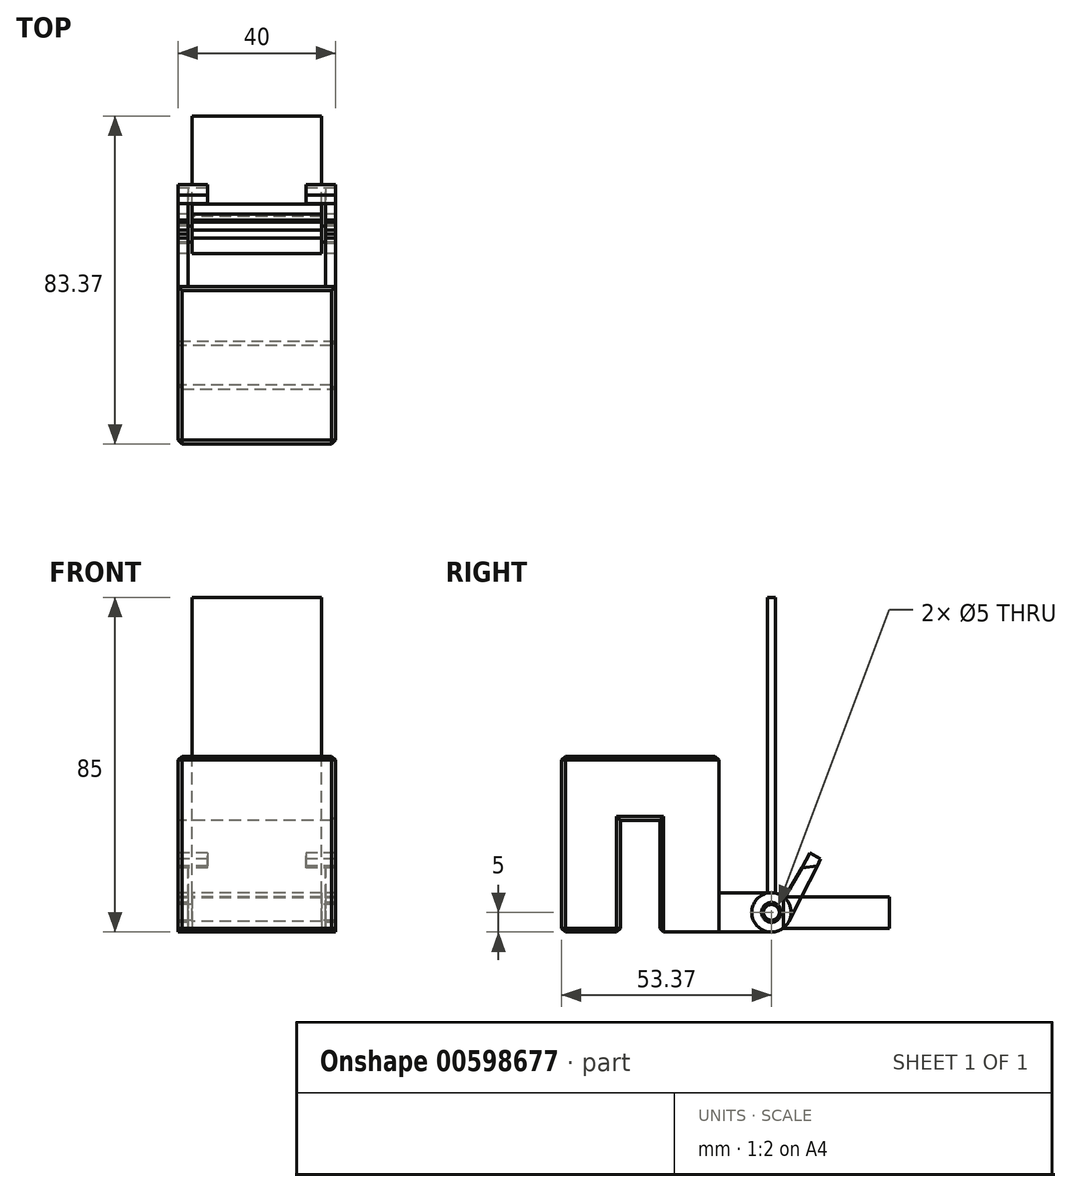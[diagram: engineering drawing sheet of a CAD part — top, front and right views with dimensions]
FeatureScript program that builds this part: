
annotation { "Feature Type Name" : "Feature", "Feature Type Description" : "" }
export const myFeature = defineFeature(function(context is Context, id is Id, definition is map)
    precondition{}
    {
        {
            var Q0;
            Q0=qCreatedBy(makeId("Right.planeOp"),FACE);
            var sketch = newSketch(context, id + "F0", { "sketchPlane" : qUnion([Q0])});
            skCircle(sketch, "E0", {"center": v(0, 0) * mm, "radius": 2.5 * mm});
            skArc(sketch, "E1", {"start": v(0, -5) * mm, "mid": v(5, 0) * mm, "end": v(0, 5) * mm});
            skLineSegment(sketch, "E2.bottom", {"start": v(0, 5) * mm, "end": v(-13.37, 5) * mm});
            skLineSegment(sketch, "E2.top", {"start": v(0, -5) * mm, "end": v(-28.37, -5) * mm});
            skLineSegment(sketch, "E2.right", {"start": v(-53.37, 5) * mm, "end": v(-53.37, -5) * mm});
            skLineSegment(sketch, "E3.top", {"start": v(-53.37, 39.68) * mm, "end": v(-13.37, 39.68) * mm});
            skLineSegment(sketch, "E3.left", {"start": v(-53.37, 5) * mm, "end": v(-53.37, 39.68) * mm});
            skLineSegment(sketch, "E3.right", {"start": v(-13.37, 5) * mm, "end": v(-13.37, 39.68) * mm});
            skLineSegment(sketch, "E4.top", {"start": v(-38.37, 23.37) * mm, "end": v(-28.37, 23.37) * mm});
            skLineSegment(sketch, "E4.left", {"start": v(-38.37, -5) * mm, "end": v(-38.37, 23.37) * mm});
            skLineSegment(sketch, "E4.right", {"start": v(-28.37, -5) * mm, "end": v(-28.37, 23.37) * mm});
            skLineSegment(sketch, "E5.trimOffspring", {"start": v(-38.37, -5) * mm, "end": v(-53.37, -5) * mm});
            skLineSegment(sketch, "E6", {"start": v(-38.37, 23.37) * mm, "end": v(-53.37, 23.37) * mm, "construction": true});
            skLineSegment(sketch, "E7", {"start": v(-28.37, 23.37) * mm, "end": v(-13.37, 23.37) * mm, "construction": true});
            skCircle(sketch, "E8", {"center": v(0, 0) * mm, "radius": 5 * mm});
            skLineSegment(sketch, "E9.bottom", {"start": v(1, 4.9) * mm, "end": v(-1, 4.9) * mm});
            skLineSegment(sketch, "E9.top", {"start": v(1, 80) * mm, "end": v(-1, 80) * mm});
            skLineSegment(sketch, "E9.left", {"start": v(1, 4.9) * mm, "end": v(1, 80) * mm});
            skLineSegment(sketch, "E9.right", {"start": v(-1, 4.9) * mm, "end": v(-1, 80) * mm});
            skPoint(sketch, "E9.middle", {"position": v(0, 42.45) * mm});
            skLineSegment(sketch, "E10.bottom", {"start": v(3, 4) * mm, "end": v(30, 4) * mm});
            skLineSegment(sketch, "E10.top", {"start": v(3, -4) * mm, "end": v(30, -4) * mm});
            skLineSegment(sketch, "E10.left", {"start": v(3, 4) * mm, "end": v(3, -4) * mm});
            skLineSegment(sketch, "E10.right", {"start": v(30, 4) * mm, "end": v(30, -4) * mm});
            skPoint(sketch, "E10.middle", {"position": v(16.5, 0) * mm});
            skCircle(sketch, "E11", {"center": v(0, 0) * mm, "radius": 2 * mm});
            skLineSegment(sketch, "E12", {"start": v(-13.37, 5) * mm, "end": v(-13.37, -5) * mm});
            skLineSegment(sketch, "E13", {"start": v(0, 0) * mm, "end": v(9.94, 17.21) * mm, "construction": true});
            skLineSegment(sketch, "E14", {"start": v(3.32, 3.74) * mm, "end": v(9.85, 15.06) * mm});
            skLineSegment(sketch, "E15", {"start": v(6.53, 11.32) * mm, "end": v(7.4, 10.82) * mm, "construction": true});
            skLineSegment(sketch, "E16", {"start": v(1, 16.02) * mm, "end": v(0, 16.02) * mm, "construction": true});
            skLineSegment(sketch, "E17", {"start": v(9.85, 15.06) * mm, "end": v(12.5, 13.53) * mm});
            skLineSegment(sketch, "E18", {"start": v(12.5, 13.53) * mm, "end": v(4.46, -2.27) * mm});
            skLineSegment(sketch, "E19", {"start": v(7.7, 11.33) * mm, "end": v(11.64, 11.85) * mm});
            skSolve(sketch);
        }
        {
            var Q0;
            {var subQ4=sQuery(id+"F0.wireOp",EDGE,"E2.top");Q0=makeQuery(id+"F0.imprint","IMPRINT",FACE,{"disambiguationData":[TD([[makeQuery(id+"F0.imprint","IMPRINT",EDGE,{"derivedFrom":subQ4}),-1.0]])]});}
            var Q1;
            Q1=makeQuery(id+"F0.imprint","IMPRINT",FACE,{"disambiguationData":[TD([[makeQuery(id+"F0.imprint","IMPRINT",EDGE,{"derivedFrom":sQuery(id+"F0.wireOp",EDGE,"E0")}),-1.0]])]});
            var Q2;
            {var subQ2=sQuery(id+"F0.wireOp",EDGE,"E9.bottom");Q2=makeQuery(id+"F0.imprint","IMPRINT",FACE,{"disambiguationData":[TD([[makeQuery(id+"F0.imprint","IMPRINT",EDGE,{"derivedFrom":subQ2}),-1.0]])]});}
            var Q3;
            {var subQ0=sQuery(id+"F0.wireOp",EDGE,"E8");var subQ1=sQuery(id+"F0.wireOp",EDGE,"E2.bottom");var subQ2=makeQuery(id+"F0.imprint","INTERSECT",VERTEX,{"derivedFrom":[subQ1,subQ0]});Q3=makeQuery(id+"F0.imprint","IMPRINT",FACE,{"disambiguationData":[TD([[makeQuery(id+"F0.imprint","IMPRINT",EDGE,{"disambiguationData":[TD([[subQ2,-1.0]])],"derivedFrom":subQ1}),1.0]])]});}
            var Q4;
            {var subQ0=sQuery(id+"F0.wireOp",EDGE,"E10.left");Q4=makeQuery(id+"F0.imprint","IMPRINT",FACE,{"disambiguationData":[TD([[makeQuery(id+"F0.imprint","IMPRINT",EDGE,{"derivedFrom":subQ0}),1.0]])]});}
            var Q5;
            Q5=makeQuery(id+"F0.imprint","IMPRINT",FACE,{"disambiguationData":[TD([[makeQuery(id+"F0.imprint","IMPRINT",EDGE,{"derivedFrom":sQuery(id+"F0.wireOp",EDGE,"E2.right")}),1.0]])]});
            var Q6;
            {var subQ1=sQuery(id+"F0.wireOp",EDGE,"E8");var subQ3=sQuery(id+"F0.wireOp",EDGE,"pCUO0WgF-IgAN-LRAv-omMa-FBrBm6pz1iVL");var subQ4=makeQuery(id+"F0.imprint","INTERSECT",VERTEX,{"derivedFrom":[subQ1,subQ3]});Q6=makeQuery(id+"F0.imprint","IMPRINT",FACE,{"disambiguationData":[TD([[makeQuery(id+"F0.imprint","IMPRINT",EDGE,{"disambiguationData":[TD([[subQ4,1.0]])],"derivedFrom":subQ3}),-1.0]])]});}
            var Q7;
            {var subQ0=sQuery(id+"F0.wireOp",EDGE,"0aa6f748-86be-4359-a253-0a0e9de2a2ff.0");Q7=makeQuery(id+"F0.imprint","IMPRINT",FACE,{"disambiguationData":[TD([[makeQuery(id+"F0.imprint","IMPRINT",EDGE,{"derivedFrom":subQ0}),-1.0]])]});}
            var Q8;
            {var subQ0=sQuery(id+"F0.wireOp",EDGE,"HSa4Dfjx-L4mI-NIt9-n0gS-I4i8fd6hyLie");Q8=makeQuery(id+"F0.imprint","IMPRINT",FACE,{"disambiguationData":[TD([[makeQuery(id+"F0.imprint","IMPRINT",EDGE,{"derivedFrom":subQ0}),-1.0]])]});}
            var Q9;
            {var subQ1=sQuery(id+"F0.wireOp",EDGE,"E8");var subQ3=sQuery(id+"F0.wireOp",EDGE,"E14");var subQ4=makeQuery(id+"F0.imprint","INTERSECT",VERTEX,{"derivedFrom":[subQ1,subQ3]});Q9=makeQuery(id+"F0.imprint","IMPRINT",FACE,{"disambiguationData":[TD([[makeQuery(id+"F0.imprint","IMPRINT",EDGE,{"disambiguationData":[TD([[subQ4,-1.0]])],"derivedFrom":subQ3}),1.0]])]});}
            var Q10;
            {var subQ0=sQuery(id+"F0.wireOp",EDGE,"E14");var subQ1=sQuery(id+"F0.wireOp",EDGE,"E8");var subQ2=makeQuery(id+"F0.imprint","INTERSECT",VERTEX,{"derivedFrom":[subQ1,subQ0]});Q10=makeQuery(id+"F0.imprint","IMPRINT",FACE,{"disambiguationData":[TD([[makeQuery(id+"F0.imprint","IMPRINT",EDGE,{"disambiguationData":[TD([[subQ2,1.0]])],"derivedFrom":subQ1}),-1.0]])]});}
            var Q11;
            {var subQ5=sQuery(id+"F0.wireOp",EDGE,"E17");Q11=makeQuery(id+"F0.imprint","IMPRINT",FACE,{"disambiguationData":[TD([[makeQuery(id+"F0.imprint","IMPRINT",EDGE,{"derivedFrom":subQ5}),-1.0]])]});}
            var Q12;
            {var subQ5=sQuery(id+"F0.wireOp",EDGE,"E19");Q12=makeQuery(id+"F0.imprint","IMPRINT",FACE,{"disambiguationData":[TD([[makeQuery(id+"F0.imprint","IMPRINT",EDGE,{"derivedFrom":subQ5}),-1.0]])]});}
            extrude(context, id + "F1", {"entities" : qUnion([Q0, Q1, Q2, Q3, Q4, Q5, Q6, Q7, Q8, Q9, Q10, Q11, Q12]), "depth" : 40 * mm, "offsetDistance" : 25 * mm, "symmetric" : true});
        }
        {
            var Q0;
            {var subQ5=sQuery(id+"F0.wireOp",EDGE,"E12");Q0=makeQuery(id+"F0.imprint","IMPRINT",FACE,{"disambiguationData":[TD([[makeQuery(id+"F0.imprint","IMPRINT",EDGE,{"derivedFrom":subQ5}),1.0]])]});}
            var Q1;
            Q1=makeQuery(id+"F0.imprint","IMPRINT",FACE,{"disambiguationData":[TD([[makeQuery(id+"F0.imprint","IMPRINT",EDGE,{"derivedFrom":sQuery(id+"F0.wireOp",EDGE,"E0")}),-1.0]])]});
            var Q2;
            {var subQ0=sQuery(id+"F0.wireOp",EDGE,"E8");var subQ1=sQuery(id+"F0.wireOp",EDGE,"E2.bottom");var subQ2=makeQuery(id+"F0.imprint","INTERSECT",VERTEX,{"derivedFrom":[subQ1,subQ0]});Q2=makeQuery(id+"F0.imprint","IMPRINT",FACE,{"disambiguationData":[TD([[makeQuery(id+"F0.imprint","IMPRINT",EDGE,{"disambiguationData":[TD([[subQ2,-1.0]])],"derivedFrom":subQ1}),1.0]])]});}
            var Q3;
            {var subQ2=sQuery(id+"F0.wireOp",EDGE,"E9.bottom");Q3=makeQuery(id+"F0.imprint","IMPRINT",FACE,{"disambiguationData":[TD([[makeQuery(id+"F0.imprint","IMPRINT",EDGE,{"derivedFrom":subQ2}),-1.0]])]});}
            var Q4;
            {var subQ0=sQuery(id+"F0.wireOp",EDGE,"E10.left");Q4=makeQuery(id+"F0.imprint","IMPRINT",FACE,{"disambiguationData":[TD([[makeQuery(id+"F0.imprint","IMPRINT",EDGE,{"derivedFrom":subQ0}),1.0]])]});}
            var Q5;
            {var subQ1=sQuery(id+"F0.wireOp",EDGE,"E8");var subQ3=sQuery(id+"F0.wireOp",EDGE,"pCUO0WgF-IgAN-LRAv-omMa-FBrBm6pz1iVL");var subQ4=makeQuery(id+"F0.imprint","INTERSECT",VERTEX,{"derivedFrom":[subQ1,subQ3]});Q5=makeQuery(id+"F0.imprint","IMPRINT",FACE,{"disambiguationData":[TD([[makeQuery(id+"F0.imprint","IMPRINT",EDGE,{"disambiguationData":[TD([[subQ4,1.0]])],"derivedFrom":subQ3}),-1.0]])]});}
            var Q6;
            {var subQ0=sQuery(id+"F0.wireOp",EDGE,"0aa6f748-86be-4359-a253-0a0e9de2a2ff.0");Q6=makeQuery(id+"F0.imprint","IMPRINT",FACE,{"disambiguationData":[TD([[makeQuery(id+"F0.imprint","IMPRINT",EDGE,{"derivedFrom":subQ0}),-1.0]])]});}
            var Q7;
            {var subQ5=sQuery(id+"F0.wireOp",EDGE,"E19");Q7=makeQuery(id+"F0.imprint","IMPRINT",FACE,{"disambiguationData":[TD([[makeQuery(id+"F0.imprint","IMPRINT",EDGE,{"derivedFrom":subQ5}),-1.0]])]});}
            var Q8;
            {var subQ0=sQuery(id+"F0.wireOp",EDGE,"E14");var subQ1=sQuery(id+"F0.wireOp",EDGE,"E8");var subQ2=makeQuery(id+"F0.imprint","INTERSECT",VERTEX,{"derivedFrom":[subQ1,subQ0]});Q8=makeQuery(id+"F0.imprint","IMPRINT",FACE,{"disambiguationData":[TD([[makeQuery(id+"F0.imprint","IMPRINT",EDGE,{"disambiguationData":[TD([[subQ2,1.0]])],"derivedFrom":subQ1}),-1.0]])]});}
            var Q9;
            {var subQ1=sQuery(id+"F0.wireOp",EDGE,"E8");var subQ3=sQuery(id+"F0.wireOp",EDGE,"E14");var subQ4=makeQuery(id+"F0.imprint","INTERSECT",VERTEX,{"derivedFrom":[subQ1,subQ3]});Q9=makeQuery(id+"F0.imprint","IMPRINT",FACE,{"disambiguationData":[TD([[makeQuery(id+"F0.imprint","IMPRINT",EDGE,{"disambiguationData":[TD([[subQ4,-1.0]])],"derivedFrom":subQ3}),1.0]])]});}
            extrude(context, id + "F2", {"entities" : qUnion([Q0, Q1, Q2, Q3, Q4, Q5, Q6, Q7, Q8, Q9]), "operationType" : NewBodyOperationType.REMOVE, "depth" : 35 * mm, "offsetDistance" : 25 * mm, "symmetric" : true});
        }
        {
            var Q0;
            {var subQ0=sQuery(id+"F0.wireOp",EDGE,"E9.top");Q0=makeQuery(id+"F0.imprint","IMPRINT",FACE,{"disambiguationData":[TD([[makeQuery(id+"F0.imprint","IMPRINT",EDGE,{"derivedFrom":subQ0}),1.0]])]});}
            var Q1;
            {var subQ0=sQuery(id+"F0.wireOp",EDGE,"E8");var subQ1=sQuery(id+"F0.wireOp",EDGE,"E2.bottom");var subQ2=makeQuery(id+"F0.imprint","INTERSECT",VERTEX,{"derivedFrom":[subQ1,subQ0]});Q1=makeQuery(id+"F0.imprint","IMPRINT",FACE,{"disambiguationData":[TD([[makeQuery(id+"F0.imprint","IMPRINT",EDGE,{"disambiguationData":[TD([[subQ2,-1.0]])],"derivedFrom":subQ1}),1.0]])]});}
            var Q2;
            {var subQ2=sQuery(id+"F0.wireOp",EDGE,"E9.bottom");Q2=makeQuery(id+"F0.imprint","IMPRINT",FACE,{"disambiguationData":[TD([[makeQuery(id+"F0.imprint","IMPRINT",EDGE,{"derivedFrom":subQ2}),-1.0]])]});}
            var Q3;
            Q3=makeQuery(id+"F0.imprint","IMPRINT",FACE,{"disambiguationData":[TD([[makeQuery(id+"F0.imprint","IMPRINT",EDGE,{"derivedFrom":sQuery(id+"F0.wireOp",EDGE,"E0")}),-1.0]])]});
            var Q4;
            {var subQ0=sQuery(id+"F0.wireOp",EDGE,"E10.left");Q4=makeQuery(id+"F0.imprint","IMPRINT",FACE,{"disambiguationData":[TD([[makeQuery(id+"F0.imprint","IMPRINT",EDGE,{"derivedFrom":subQ0}),1.0]])]});}
            var Q5;
            Q5=makeQuery(id+"F0.imprint","IMPRINT",FACE,{"disambiguationData":[TD([[makeQuery(id+"F0.imprint","IMPRINT",EDGE,{"derivedFrom":sQuery(id+"F0.wireOp",EDGE,"E0")}),1.0]])]});
            var Q6;
            Q6=makeQuery(id+"F0.imprint","IMPRINT",FACE,{"disambiguationData":[TD([[makeQuery(id+"F0.imprint","IMPRINT",EDGE,{"derivedFrom":sQuery(id+"F0.wireOp",EDGE,"E11")}),1.0]])]});
            var Q7;
            {var subQ1=sQuery(id+"F0.wireOp",EDGE,"E10.top");Q7=makeQuery(id+"F0.imprint","IMPRINT",FACE,{"disambiguationData":[TD([[makeQuery(id+"F0.imprint","IMPRINT",EDGE,{"derivedFrom":subQ1}),1.0]])]});}
            var Q8;
            {var subQ0=sQuery(id+"F0.wireOp",EDGE,"E14");var subQ1=sQuery(id+"F0.wireOp",EDGE,"E8");var subQ2=makeQuery(id+"F0.imprint","INTERSECT",VERTEX,{"derivedFrom":[subQ1,subQ0]});Q8=makeQuery(id+"F0.imprint","IMPRINT",FACE,{"disambiguationData":[TD([[makeQuery(id+"F0.imprint","IMPRINT",EDGE,{"disambiguationData":[TD([[subQ2,1.0]])],"derivedFrom":subQ1}),-1.0]])]});}
            var Q9;
            {var subQ1=sQuery(id+"F0.wireOp",EDGE,"E8");var subQ3=sQuery(id+"F0.wireOp",EDGE,"E14");var subQ4=makeQuery(id+"F0.imprint","INTERSECT",VERTEX,{"derivedFrom":[subQ1,subQ3]});Q9=makeQuery(id+"F0.imprint","IMPRINT",FACE,{"disambiguationData":[TD([[makeQuery(id+"F0.imprint","IMPRINT",EDGE,{"disambiguationData":[TD([[subQ4,-1.0]])],"derivedFrom":subQ3}),1.0]])]});}
            extrude(context, id + "F3", {"entities" : qUnion([Q0, Q1, Q2, Q3, Q4, Q5, Q6, Q7, Q8, Q9]), "depth" : 33 * mm, "offsetDistance" : 25 * mm, "symmetric" : true});
        }
        {
            var Q0;
            Q0=makeQuery(id+"F0.imprint","IMPRINT",FACE,{"disambiguationData":[TD([[makeQuery(id+"F0.imprint","IMPRINT",EDGE,{"derivedFrom":sQuery(id+"F0.wireOp",EDGE,"E11")}),1.0]])]});
            var Q1;
            Q1=sQuery(id+"F0.wireOp",EDGE,"E11");
            extrude(context, id + "F4", {"entities" : qUnion([Q0]), "operationType" : NewBodyOperationType.ADD, "surfaceEntities" : qUnion([Q1]), "depth" : 40 * mm, "offsetDistance" : 25 * mm, "symmetric" : true});
        }
        {
            var Q0;
            {var subQ0=sQuery(id+"F0.wireOp",EDGE,"E17");Q0=makeQuery(id+"F0.imprint","IMPRINT",FACE,{"disambiguationData":[TD([[makeQuery(id+"F0.imprint","IMPRINT",EDGE,{"derivedFrom":subQ0}),-1.0]])]});}
            extrude(context, id + "F5", {"entities" : qUnion([Q0]), "operationType" : NewBodyOperationType.REMOVE, "depth" : 25 * mm, "offsetDistance" : 25 * mm, "symmetric" : true});
        }
        {
            var Q0;
            Q0=makeQuery(id+"F1.opExtrude","SWEPT_EDGE",EDGE,{"disambiguationData":[OSD([sQuery(id+"F0.wireOp",EDGE,"E3.top"),sQuery(id+"F0.wireOp",EDGE,"E3.left")])]});
            var Q1;
            Q1=makeQuery(id+"F1.opExtrude","CAP_EDGE",EDGE,{"disambiguationData":[OSD([sQuery(id+"F0.wireOp",EDGE,"E3.top")])],"isStart":false});
            var Q2;
            Q2=makeQuery(id+"F1.opExtrude","SWEPT_EDGE",EDGE,{"disambiguationData":[OSD([sQuery(id+"F0.wireOp",EDGE,"E3.top"),sQuery(id+"F0.wireOp",EDGE,"E3.right")])]});
            var Q3;
            Q3=makeQuery(id+"F1.opExtrude","CAP_EDGE",EDGE,{"disambiguationData":[OSD([sQuery(id+"F0.wireOp",EDGE,"E3.top")])],"isStart":true});
            var Q4;
            Q4=makeQuery(id+"F1.opExtrude","CAP_EDGE",EDGE,{"disambiguationData":[OSD([sQuery(id+"F0.wireOp",EDGE,"E2.right"),sQuery(id+"F0.wireOp",EDGE,"E3.left")])],"isStart":false});
            var Q5;
            Q5=makeQuery(id+"F1.opExtrude","CAP_EDGE",EDGE,{"disambiguationData":[OSD([sQuery(id+"F0.wireOp",EDGE,"E5.trimOffspring")])],"isStart":false});
            var Q6;
            Q6=makeQuery(id+"F1.opExtrude","SWEPT_EDGE",EDGE,{"disambiguationData":[OSD([sQuery(id+"F0.wireOp",EDGE,"E4.left"),sQuery(id+"F0.wireOp",EDGE,"E5.trimOffspring")])]});
            var Q7;
            Q7=makeQuery(id+"F1.opExtrude","SWEPT_EDGE",EDGE,{"disambiguationData":[OSD([sQuery(id+"F0.wireOp",EDGE,"E2.top"),sQuery(id+"F0.wireOp",EDGE,"E4.right")])]});
            var Q8;
            Q8=makeQuery(id+"F1.opExtrude","CAP_EDGE",EDGE,{"disambiguationData":[OSD([sQuery(id+"F0.wireOp",EDGE,"E4.left")])],"isStart":false});
            var Q9;
            Q9=makeQuery(id+"F1.opExtrude","CAP_EDGE",EDGE,{"disambiguationData":[OSD([sQuery(id+"F0.wireOp",EDGE,"E4.top")])],"isStart":false});
            var Q10;
            Q10=makeQuery(id+"F1.opExtrude","CAP_EDGE",EDGE,{"disambiguationData":[OSD([sQuery(id+"F0.wireOp",EDGE,"E4.right")])],"isStart":false});
            var Q11;
            Q11=makeQuery(id+"F1.opExtrude","SWEPT_EDGE",EDGE,{"disambiguationData":[OSD([sQuery(id+"F0.wireOp",EDGE,"E2.right"),sQuery(id+"F0.wireOp",EDGE,"E5.trimOffspring")])]});
            var Q12;
            Q12=makeQuery(id+"F1.opExtrude","CAP_EDGE",EDGE,{"disambiguationData":[OSD([sQuery(id+"F0.wireOp",EDGE,"E5.trimOffspring")])],"isStart":true});
            var Q13;
            Q13=makeQuery(id+"F1.opExtrude","CAP_EDGE",EDGE,{"disambiguationData":[OSD([sQuery(id+"F0.wireOp",EDGE,"E2.right"),sQuery(id+"F0.wireOp",EDGE,"E3.left")])],"isStart":true});
            chamfer(context, id + "F6", {"entities" : qUnion([Q0, Q1, Q2, Q3, Q4, Q5, Q6, Q7, Q8, Q9, Q10, Q11, Q12, Q13]), "width" : 1 * mm, "tangentPropagation" : true});
        }
    });
